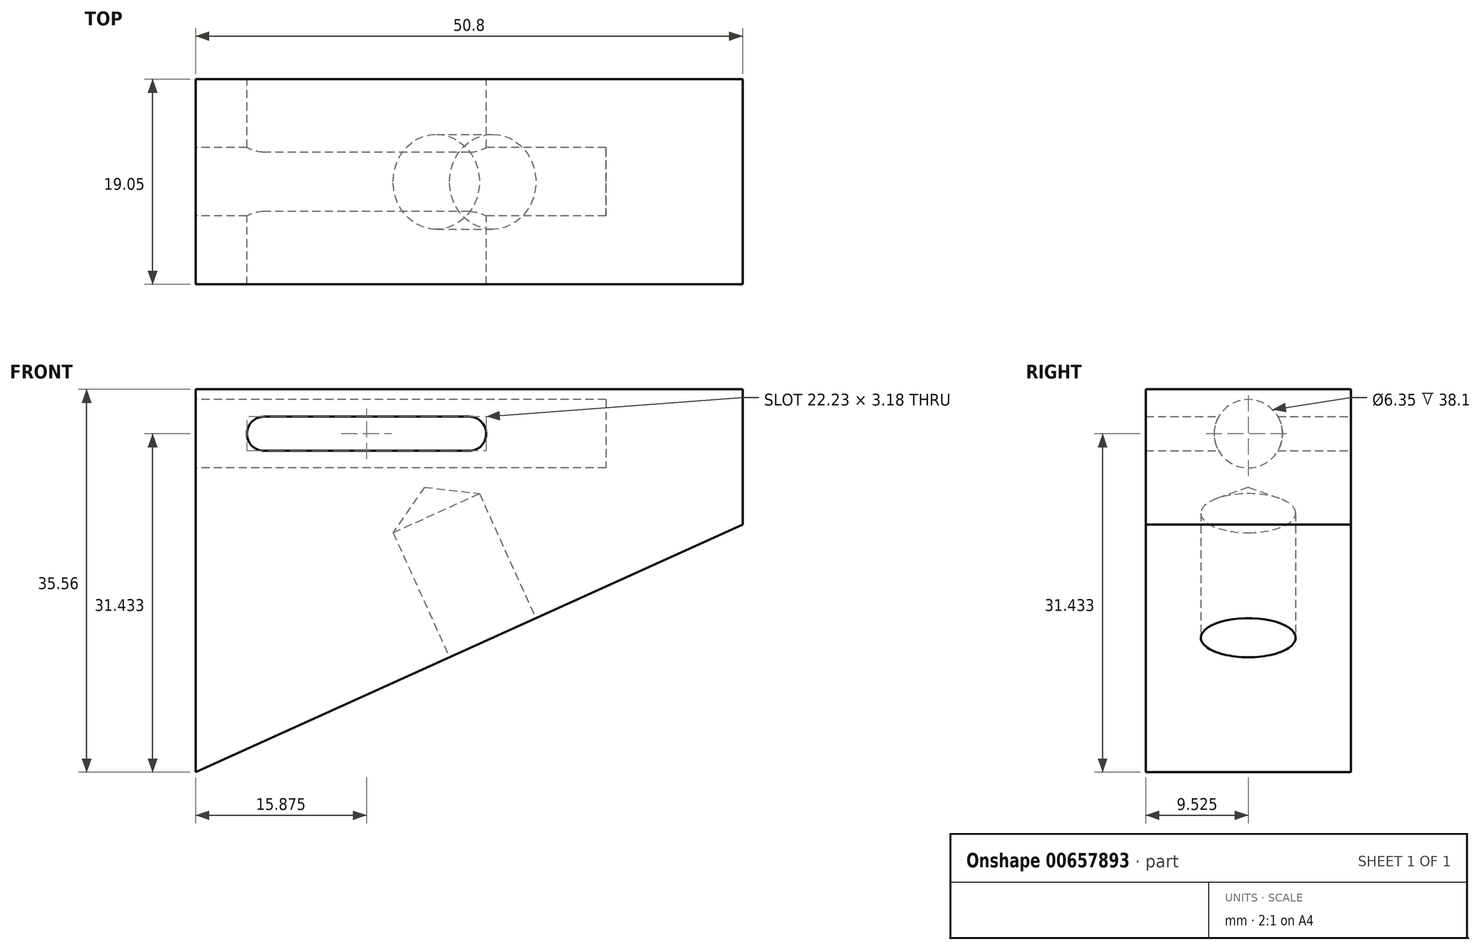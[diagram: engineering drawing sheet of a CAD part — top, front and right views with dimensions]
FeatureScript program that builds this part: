
annotation { "Feature Type Name" : "Feature", "Feature Type Description" : "" }
export const myFeature = defineFeature(function(context is Context, id is Id, definition is map)
    precondition{}
    {
        {
            var Q0;
            Q0=qCreatedBy(makeId("Front.planeOp"),FACE);
            var sketch = newSketch(context, id + "F0", { "sketchPlane" : qUnion([Q0])});
            skLineSegment(sketch, "E0", {"start": v(-20.67, -27.76) * mm, "end": v(-20.67, 7.8) * mm});
            skLineSegment(sketch, "E1", {"start": v(-20.67, 7.8) * mm, "end": v(30.13, 7.8) * mm});
            skLineSegment(sketch, "E2", {"start": v(30.13, 7.8) * mm, "end": v(30.13, -4.75) * mm});
            skLineSegment(sketch, "E3", {"start": v(30.13, -4.75) * mm, "end": v(-20.67, -27.76) * mm});
            skLineSegment(sketch, "E4", {"start": v(-14.32, 3.67) * mm, "end": v(4.73, 3.67) * mm, "construction": true});
            skArc(sketch, "E5.0.startCap", {"start": v(-14.32, 2.09) * mm, "mid": v(-15.9, 3.67) * mm, "end": v(-14.32, 5.26) * mm, "construction": true});
            skArc(sketch, "E5.0.endCap", {"start": v(4.73, 5.26) * mm, "mid": v(6.32, 3.67) * mm, "end": v(4.73, 2.09) * mm, "construction": true});
            skLineSegment(sketch, "E5.0.left", {"start": v(-14.32, 5.26) * mm, "end": v(4.73, 5.26) * mm, "construction": true});
            skLineSegment(sketch, "E5.0.right", {"start": v(-14.32, 2.09) * mm, "end": v(4.73, 2.09) * mm, "construction": true});
            skSolve(sketch);
        }
        {
            var Q0;
            Q0=makeQuery(id+"F0.imprint","IMPRINT",FACE,{"disambiguationData":[TD([[makeQuery(id+"F0.imprint","IMPRINT",EDGE,{"derivedFrom":sQuery(id+"F0.wireOp",EDGE,"E0")}),-1.0]])]});
            extrude(context, id + "F1", {"entities" : qUnion([Q0]), "depth" : 19.05 * mm, "offsetDistance" : 25.4 * mm});
        }
        {
            var Q0;
            Q0=makeQuery(id+"F1.opExtrude","SWEPT_FACE",FACE,{"disambiguationData":[OSD([sQuery(id+"F0.wireOp",EDGE,"E1")])]});
            var Q1;
            Q1=sQuery(id+"F0.wireOp",VERTEX,"E4.start");
            cPlane(context, id + "F2", {"entities" : qUnion([Q0, Q1]), "cplaneType" : CPlaneType.PLANE_POINT, "offset" : 0 * mm, "width" : 152.4 * mm, "height" : 152.4 * mm});
        }
        {
            var Q0;
            Q0=makeQuery(id+"F1.opExtrude","SWEPT_FACE",FACE,{"disambiguationData":[OSD([sQuery(id+"F0.wireOp",EDGE,"E0")])]});
            var sketch = newSketch(context, id + "F3", { "sketchPlane" : qUnion([Q0])});
            skLineSegment(sketch, "E6", {"start": v(9.53, 7.8) * mm, "end": v(9.53, -27.76) * mm, "construction": true});
            skLineSegment(sketch, "E7", {"start": v(5.17, 3.67) * mm, "end": v(14.33, 3.67) * mm, "construction": true});
            skCircle(sketch, "E8", {"center": v(9.53, 3.67) * mm, "radius": 3.18 * mm});
            skSolve(sketch);
        }
        {
            var Q0;
            Q0=makeQuery(id+"F3.imprint","IMPRINT",FACE,{"disambiguationData":[TD([[makeQuery(id+"F3.imprint","IMPRINT",EDGE,{"derivedFrom":sQuery(id+"F3.wireOp",EDGE,"E8")}),1.0]])]});
            var Q1;
            Q1=sQuery(id+"F3.wireOp",EDGE,"E8");
            extrude(context, id + "F4", {"entities" : qUnion([Q0]), "operationType" : NewBodyOperationType.REMOVE, "surfaceEntities" : qUnion([Q1]), "oppositeDirection" : true, "depth" : 38.1 * mm, "offsetDistance" : 25.4 * mm});
        }
        {
            var Q0;
            Q0=makeQuery(id+"F0.imprint","IMPRINT",FACE,{"disambiguationData":[TD([[makeQuery(id+"F0.imprint","IMPRINT",EDGE,{"derivedFrom":sQuery(id+"F0.wireOp",EDGE,"E0")}),-1.0]])]});
            var sketch = newSketch(context, id + "F5", { "sketchPlane" : qUnion([Q0])});
            skLineSegment(sketch, "E9", {"start": v(4.73, 3.67) * mm, "end": v(-14.32, 3.67) * mm, "construction": true});
            skArc(sketch, "E10.0.startCap", {"start": v(4.73, 5.26) * mm, "mid": v(6.32, 3.67) * mm, "end": v(4.73, 2.09) * mm});
            skArc(sketch, "E10.0.endCap", {"start": v(-14.32, 2.09) * mm, "mid": v(-15.9, 3.67) * mm, "end": v(-14.32, 5.26) * mm});
            skLineSegment(sketch, "E10.0.left", {"start": v(4.73, 2.09) * mm, "end": v(-14.32, 2.09) * mm});
            skLineSegment(sketch, "E10.0.right", {"start": v(4.73, 5.26) * mm, "end": v(-14.32, 5.26) * mm});
            skSolve(sketch);
        }
        {
            var Q0;
            Q0 = qSketchRegion(id + "F5", true);
            var Q1;
            Q1=makeQuery(id+"F1.opExtrude","CAP_FACE",FACE,{"disambiguationData":[OSD([sQuery(id+"F0.wireOp",EDGE,"E0"),sQuery(id+"F0.wireOp",EDGE,"E1"),sQuery(id+"F0.wireOp",EDGE,"E2"),sQuery(id+"F0.wireOp",EDGE,"E3")])],"isStart":false});
            extrude(context, id + "F6", {"entities" : qUnion([Q0]), "operationType" : NewBodyOperationType.REMOVE, "endBound" : BoundingType.UP_TO_SURFACE, "depth" : 25.4 * mm, "endBoundEntityFace" : qUnion([Q1]), "offsetDistance" : 25.4 * mm});
        }
        {
            var Q0;
            Q0=makeQuery(id+"F1.opExtrude","SWEPT_FACE",FACE,{"disambiguationData":[OSD([sQuery(id+"F0.wireOp",EDGE,"E3")])]});
            var sketch = newSketch(context, id + "F7", { "sketchPlane" : qUnion([Q0])});
            skLineSegment(sketch, "E11", {"start": v(-30.28, 9.53) * mm, "end": v(0, 9.53) * mm, "construction": true});
            skLineSegment(sketch, "E12", {"start": v(0, 9.53) * mm, "end": v(0, 0) * mm, "construction": true});
            skSolve(sketch);
        }
        {
            var Q0;
            Q0=sQuery(id+"F7.wireOp",VERTEX,"E11.end");
            var Q1;
            Q1=makeQuery(id+"F1.opExtrude","SWEPT_BODY",BODY,{"disambiguationData":[OSD([sQuery(id+"F0.wireOp",EDGE,"E0"),sQuery(id+"F0.wireOp",EDGE,"E1"),sQuery(id+"F0.wireOp",EDGE,"E2"),sQuery(id+"F0.wireOp",EDGE,"E3")])]});
            hole(context, id + "F8", {"style" : HoleStyle.SIMPLE, "endStyle" : HoleEndStyle.BLIND, "standardTappedOrClearance" : lookupTablePath({ "standard" : "ISO", "fit" : "Normal", "size" : "M8", "type" : "Clearance" }), "standardBlindInLast" : lookupTablePath({ "fit" : "Standard", "standard" : "ISO", "size" : "M8", "type" : "Clearance" }), "holeDiameter" : 8.8 * mm, "majorDiameter" : 6.35 * mm, "holeDepth" : 12.7 * mm, "isTappedThrough" : true, "tappedDepth" : 12.7 * mm, "tapClearance" : 3, "locations" : qUnion([Q0]), "scope" : qUnion([Q1])});
        }
    });
